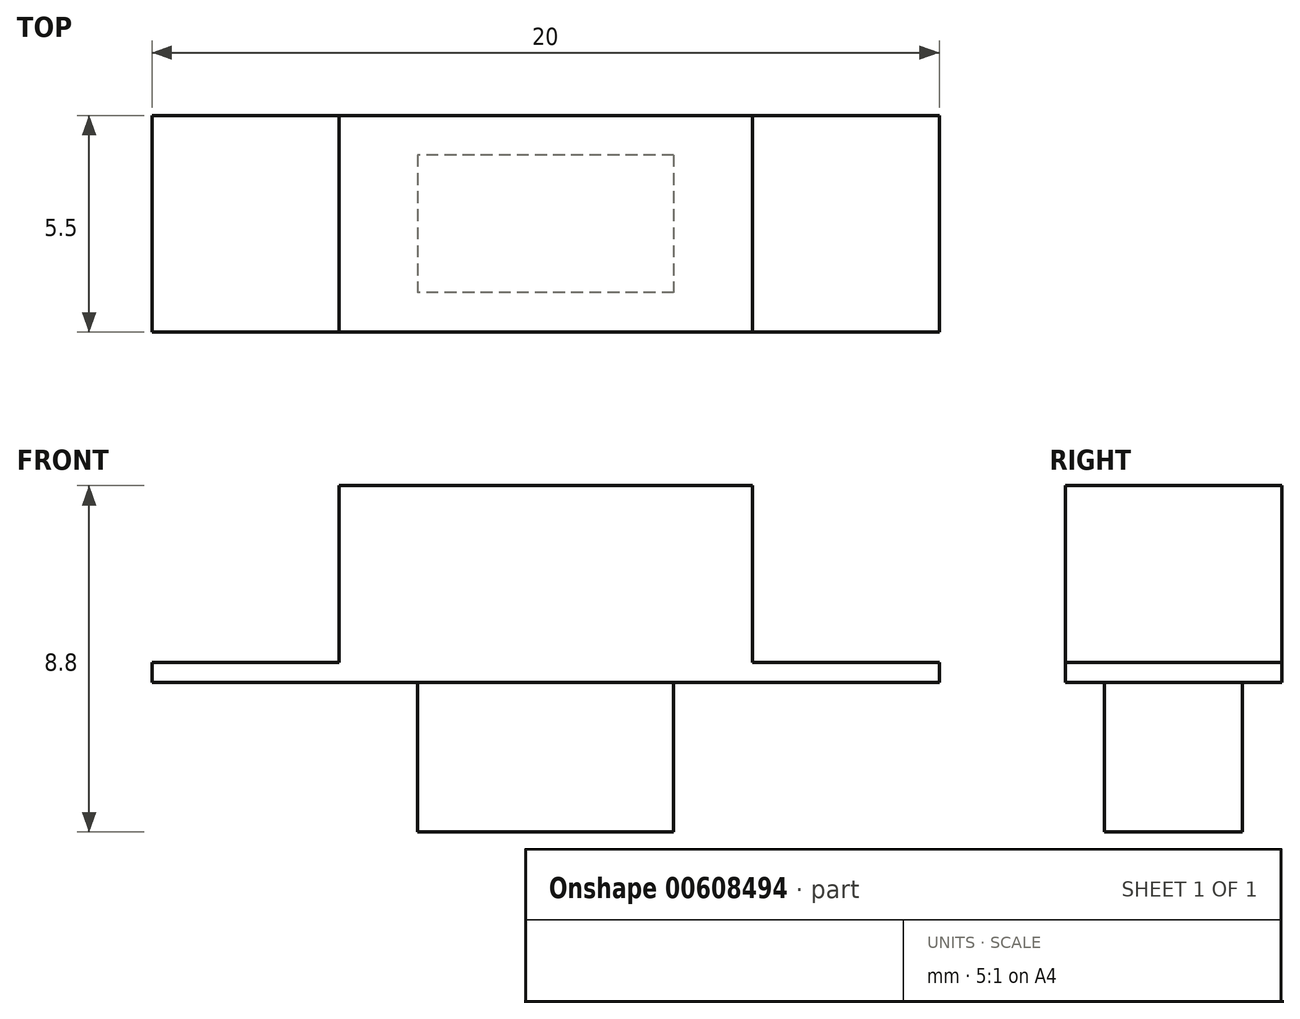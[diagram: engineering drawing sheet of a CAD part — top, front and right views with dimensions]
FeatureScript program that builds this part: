
annotation { "Feature Type Name" : "Feature", "Feature Type Description" : "" }
export const myFeature = defineFeature(function(context is Context, id is Id, definition is map)
    precondition{}
    {
        {
            var Q0;
            Q0=qCreatedBy(makeId("Top.planeOp"),FACE);
            var sketch = newSketch(context, id + "F0", { "sketchPlane" : qUnion([Q0])});
            skLineSegment(sketch, "E0.bottom", {"start": v(10, 2.75) * mm, "end": v(-10, 2.75) * mm});
            skLineSegment(sketch, "E0.top", {"start": v(10, -2.75) * mm, "end": v(-10, -2.75) * mm});
            skLineSegment(sketch, "E0.left", {"start": v(10, 2.75) * mm, "end": v(10, -2.75) * mm});
            skLineSegment(sketch, "E0.right", {"start": v(-10, 2.75) * mm, "end": v(-10, -2.75) * mm});
            skPoint(sketch, "E0.middle", {"position": v(0, 0) * mm});
            skSolve(sketch);
        }
        {
            var Q0;
            Q0 = qSketchRegion(id + "F0", true);
            extrude(context, id + "F1", {"entities" : qUnion([Q0]), "depth" : 0.5 * mm, "offsetDistance" : 25 * mm});
        }
        {
            var Q0;
            Q0=makeQuery(id+"F1.opExtrude","CAP_FACE",FACE,{"disambiguationData":[OSD([sQuery(id+"F0.wireOp",EDGE,"E0.bottom"),sQuery(id+"F0.wireOp",EDGE,"E0.top"),sQuery(id+"F0.wireOp",EDGE,"E0.left"),sQuery(id+"F0.wireOp",EDGE,"E0.right")])],"isStart":false});
            var sketch = newSketch(context, id + "F2", { "sketchPlane" : qUnion([Q0])});
            skLineSegment(sketch, "E1.bottom", {"start": v(5.25, 2.75) * mm, "end": v(-5.25, 2.75) * mm});
            skLineSegment(sketch, "E1.top", {"start": v(5.25, -2.75) * mm, "end": v(-5.25, -2.75) * mm});
            skLineSegment(sketch, "E1.left", {"start": v(5.25, 2.75) * mm, "end": v(5.25, -2.75) * mm});
            skLineSegment(sketch, "E1.right", {"start": v(-5.25, 2.75) * mm, "end": v(-5.25, -2.75) * mm});
            skPoint(sketch, "E1.middle", {"position": v(0, 0) * mm});
            skSolve(sketch);
        }
        {
            var Q0;
            Q0 = qSketchRegion(id + "F2", true);
            extrude(context, id + "F3", {"entities" : qUnion([Q0]), "operationType" : NewBodyOperationType.ADD, "depth" : 4.5 * mm, "offsetDistance" : 25 * mm});
        }
        {
            var Q0;
            Q0=makeQuery(id+"F1.opExtrude","CAP_FACE",FACE,{"disambiguationData":[OSD([sQuery(id+"F0.wireOp",EDGE,"E0.bottom"),sQuery(id+"F0.wireOp",EDGE,"E0.top"),sQuery(id+"F0.wireOp",EDGE,"E0.left"),sQuery(id+"F0.wireOp",EDGE,"E0.right")])],"isStart":true});
            var sketch = newSketch(context, id + "F4", { "sketchPlane" : qUnion([Q0])});
            skLineSegment(sketch, "E2.bottom", {"start": v(3.25, -1.75) * mm, "end": v(-3.25, -1.75) * mm});
            skLineSegment(sketch, "E2.top", {"start": v(3.25, 1.75) * mm, "end": v(-3.25, 1.75) * mm});
            skLineSegment(sketch, "E2.left", {"start": v(3.25, -1.75) * mm, "end": v(3.25, 1.75) * mm});
            skLineSegment(sketch, "E2.right", {"start": v(-3.25, -1.75) * mm, "end": v(-3.25, 1.75) * mm});
            skPoint(sketch, "E2.middle", {"position": v(0, 0) * mm});
            skSolve(sketch);
        }
        {
            var Q0;
            Q0 = qSketchRegion(id + "F4", true);
            extrude(context, id + "F5", {"entities" : qUnion([Q0]), "operationType" : NewBodyOperationType.ADD, "depth" : 3.8 * mm, "offsetDistance" : 25 * mm});
        }
    });
